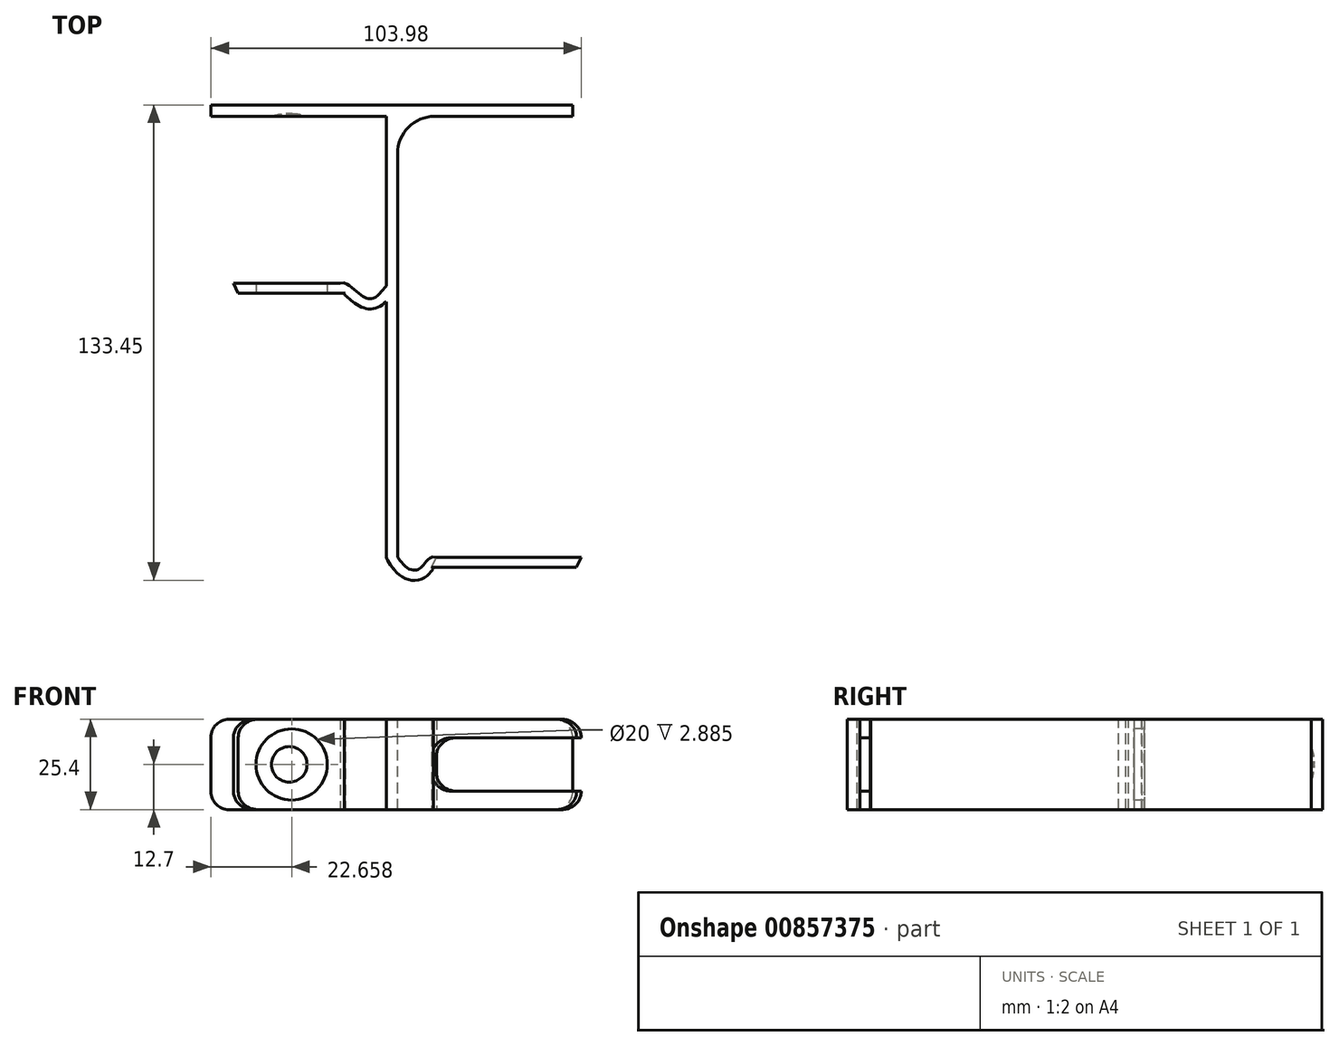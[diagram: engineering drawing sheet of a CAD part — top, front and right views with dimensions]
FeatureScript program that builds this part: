
annotation { "Feature Type Name" : "Feature", "Feature Type Description" : "" }
export const myFeature = defineFeature(function(context is Context, id is Id, definition is map)
    precondition{}
    {
        {
            var Q0;
            Q0=qCreatedBy(makeId("Top.planeOp"),FACE);
            var sketch = newSketch(context, id + "F0", { "sketchPlane" : qUnion([Q0])});
            skLineSegment(sketch, "E0.bottom", {"start": v(-50.8, 12.7) * mm, "end": v(50.8, 12.7) * mm});
            skLineSegment(sketch, "E0.top", {"start": v(-50.8, -12.7) * mm, "end": v(50.8, -12.7) * mm});
            skLineSegment(sketch, "E0.left", {"start": v(-50.8, 12.7) * mm, "end": v(-50.8, -12.7) * mm});
            skLineSegment(sketch, "E0.right", {"start": v(50.8, 12.7) * mm, "end": v(50.8, -12.7) * mm});
            skSolve(sketch);
        }
        {
            var Q0;
            Q0=makeQuery(id+"F0.imprint","IMPRINT",FACE,{"disambiguationData":[TD([[makeQuery(id+"F0.imprint","IMPRINT",EDGE,{"derivedFrom":sQuery(id+"F0.wireOp",EDGE,"E0.bottom")}),-1.0]])]});
            var sketch = newSketch(context, id + "F1", { "sketchPlane" : qUnion([Q0])});
            skLineSegment(sketch, "E1.bottom", {"start": v(-1.59, 12.7) * mm, "end": v(1.59, 12.7) * mm});
            skLineSegment(sketch, "E1.top", {"start": v(-1.59, -12.7) * mm, "end": v(1.59, -12.7) * mm});
            skLineSegment(sketch, "E1.left", {"start": v(-1.59, 12.7) * mm, "end": v(-1.59, -12.7) * mm});
            skLineSegment(sketch, "E1.right", {"start": v(1.59, 12.7) * mm, "end": v(1.59, -12.7) * mm});
            skSolve(sketch);
        }
        {
            var Q0;
            Q0=qCreatedBy(makeId("Front.planeOp"),FACE);
            var sketch = newSketch(context, id + "F2", { "sketchPlane" : qUnion([Q0])});
            skLineSegment(sketch, "E2", {"start": v(0, 0) * mm, "end": v(0, 127) * mm});
            skFitSpline(sketch, "E3", {"points": [v(0, 127) * mm, v(3.55, 131.12) * mm, v(8.81, 131.14) * mm, v(11.88, 128.39) * mm], "startDerivative": vector(1.99, 4.33) * mm, "endDerivative": vector(8.55, 0) * mm});
            skLineSegment(sketch, "E4", {"start": v(11.88, 128.39) * mm, "end": v(52.52, 128.39) * mm});
            skSolve(sketch);
        }
        {
            var Q0;
            Q0=qCreatedBy(makeId("Front.planeOp"),FACE);
            var sketch = newSketch(context, id + "F3", { "sketchPlane" : qUnion([Q0])});
            skLineSegment(sketch, "E5.MirrorCS", {"start": v(-13.8, 51.45) * mm, "end": v(-43.8, 51.45) * mm});
            skFitSpline(sketch, "E6.MirrorCS", {"points": [v(0, 50.8) * mm, v(-3.55, 54.92) * mm, v(-8.81, 54.94) * mm, v(-13.8, 51.45) * mm], "startDerivative": vector(-1.99, 4.33) * mm, "endDerivative": vector(-8.55, 0) * mm});
            skLineSegment(sketch, "E7", {"start": v(0, 50.8) * mm, "end": v(0, 0) * mm});
            skSolve(sketch);
        }
        {
            var Q0;
            Q0 = qSketchRegion(id + "F1", true);
            var Q1;
            Q1=sQuery(id+"F2.wireOp",EDGE,"E2");
            sweep(context, id + "F4", {"profiles" : qUnion([Q0]), "path" : qUnion([Q1])});
        }
        {
            var Q0;
            Q0=makeQuery(id+"F4.opSweep","CAP_FACE",FACE,{"disambiguationData":[OSD([sQuery(id+"F1.wireOp",EDGE,"E1.bottom"),sQuery(id+"F1.wireOp",EDGE,"E1.top"),sQuery(id+"F1.wireOp",EDGE,"E1.left"),sQuery(id+"F1.wireOp",EDGE,"E1.right"),sQuery(id+"F2.wireOp",VERTEX,"E2.end")])],"isStart":false});
            var Q1;
            Q1=sQuery(id+"F2.wireOp",EDGE,"E3");
            var Q2;
            Q2=sQuery(id+"F2.wireOp",EDGE,"E4");
            sweep(context, id + "F5", {"operationType" : NewBodyOperationType.ADD, "profiles" : qUnion([Q0]), "path" : qUnion([Q1, Q2])});
        }
        {
            var Q0;
            Q0 = qSketchRegion(id + "F1", true);
            var Q1;
            Q1=sQuery(id+"F3.wireOp",EDGE,"E7");
            sweep(context, id + "F6", {"profiles" : qUnion([Q0]), "path" : qUnion([Q1])});
        }
        {
            var Q0;
            Q0=makeQuery(id+"F6.opSweep","CAP_FACE",FACE,{"disambiguationData":[OSD([sQuery(id+"F1.wireOp",EDGE,"E1.bottom"),sQuery(id+"F1.wireOp",EDGE,"E1.top"),sQuery(id+"F1.wireOp",EDGE,"E1.left"),sQuery(id+"F1.wireOp",EDGE,"E1.right"),sQuery(id+"F3.wireOp",VERTEX,"E7.start")])],"isStart":false});
            var Q1;
            Q1=sQuery(id+"F3.wireOp",EDGE,"E6.MirrorCS");
            var Q2;
            Q2=sQuery(id+"F3.wireOp",EDGE,"E5.MirrorCS");
            sweep(context, id + "F7", {"operationType" : NewBodyOperationType.ADD, "profiles" : qUnion([Q0]), "path" : qUnion([Q1, Q2])});
        }
        {
            var Q0;
            Q0 = qSketchRegion(id + "F0", true);
            extrude(context, id + "F8", {"entities" : qUnion([Q0]), "depth" : 3.17 * mm, "offsetDistance" : 25.4 * mm});
        }
        {
            var Q0;
            Q0=makeQuery(id+"F7.opSweep","SWEPT_FACE",FACE,{"disambiguationData":[OSD([sQuery(id+"F1.wireOp",EDGE,"E1.right"),sQuery(id+"F3.wireOp",VERTEX,"E7.start"),sQuery(id+"F3.wireOp",EDGE,"E5.MirrorCS")])]});
            var sketch = newSketch(context, id + "F9", { "sketchPlane" : qUnion([Q0])});
            skCircle(sketch, "E8", {"center": v(-28.14, 0) * mm, "radius": 10 * mm});
            skLineSegment(sketch, "E9", {"start": v(-43.14, 0) * mm, "end": v(-13.14, 0) * mm, "construction": true});
            skSolve(sketch);
        }
        {
            var Q0;
            Q0=makeQuery(id+"F9.imprint","IMPRINT",FACE,{"disambiguationData":[TD([[makeQuery(id+"F9.imprint","IMPRINT",EDGE,{"derivedFrom":sQuery(id+"F9.wireOp",EDGE,"E8")}),1.0]])]});
            extrude(context, id + "F10", {"entities" : qUnion([Q0]), "operationType" : NewBodyOperationType.REMOVE, "oppositeDirection" : true, "depth" : 3.33 * mm, "offsetDistance" : 25.4 * mm});
        }
        {
            var Q0;
            Q0=qCreatedBy(makeId("Front.planeOp"),FACE);
            var sketch = newSketch(context, id + "F11", { "sketchPlane" : qUnion([Q0])});
            skLineSegment(sketch, "E10", {"start": v(-28.8, 51.45) * mm, "end": v(-28.8, 3.18) * mm, "construction": true});
            skSolve(sketch);
        }
        {
            var Q0;
            Q0=makeQuery(id+"F8.opExtrude","CAP_FACE",FACE,{"disambiguationData":[OSD([sQuery(id+"F0.wireOp",EDGE,"E0.bottom"),sQuery(id+"F0.wireOp",EDGE,"E0.top"),sQuery(id+"F0.wireOp",EDGE,"E0.left"),sQuery(id+"F0.wireOp",EDGE,"E0.right"),sQuery(id+"F0.wireOp",EDGE,"Ot2qKh74-6Phr-nM6u-f5VL-bmw23gvkR3ha.bottom"),sQuery(id+"F0.wireOp",EDGE,"Ot2qKh74-6Phr-nM6u-f5VL-bmw23gvkR3ha.top"),sQuery(id+"F0.wireOp",EDGE,"Ot2qKh74-6Phr-nM6u-f5VL-bmw23gvkR3ha.left"),sQuery(id+"F0.wireOp",EDGE,"Ot2qKh74-6Phr-nM6u-f5VL-bmw23gvkR3ha.right")])],"isStart":false});
            var sketch = newSketch(context, id + "F12", { "sketchPlane" : qUnion([Q0])});
            skCircle(sketch, "E11", {"center": v(-28.8, 0) * mm, "radius": 5 * mm});
            skSolve(sketch);
        }
        {
            var Q0;
            Q0=makeQuery(id+"F5.opSweep","CAP_FACE",FACE,{"disambiguationData":[OSD([sQuery(id+"F1.wireOp",EDGE,"E1.bottom"),sQuery(id+"F1.wireOp",EDGE,"E1.top"),sQuery(id+"F1.wireOp",EDGE,"E1.left"),sQuery(id+"F1.wireOp",EDGE,"E1.right"),sQuery(id+"F2.wireOp",VERTEX,"E2.end"),sQuery(id+"F2.wireOp",VERTEX,"E4.end")])],"isStart":false});
            var sketch = newSketch(context, id + "F13", { "sketchPlane" : qUnion([Q0])});
            skLineSegment(sketch, "E12.bottom", {"start": v(-7.5, 96.35) * mm, "end": v(7.5, 96.35) * mm});
            skLineSegment(sketch, "E12.top", {"start": v(-7.5, 93.17) * mm, "end": v(7.5, 93.17) * mm});
            skLineSegment(sketch, "E12.left", {"start": v(-7.5, 96.35) * mm, "end": v(-7.5, 93.17) * mm});
            skLineSegment(sketch, "E12.right", {"start": v(7.5, 96.35) * mm, "end": v(7.5, 93.17) * mm});
            skLineSegment(sketch, "E13", {"start": v(-12.7, 95.1) * mm, "end": v(-7.5, 95.1) * mm, "construction": true});
            skLineSegment(sketch, "E14", {"start": v(7.5, 95.22) * mm, "end": v(12.7, 95.22) * mm, "construction": true});
            skSolve(sketch);
        }
        {
            var Q0;
            Q0 = qSketchRegion(id + "F13", true);
            var Q1;
            Q1=sQuery(id+"F2.wireOp",EDGE,"E4");
            sweep(context, id + "F14", {"operationType" : NewBodyOperationType.REMOVE, "profiles" : qUnion([Q0]), "path" : qUnion([Q1])});
        }
        {
            var Q0;
            Q0=qCreatedBy(makeId("Front.planeOp"),FACE);
            var sketch = newSketch(context, id + "F15", { "sketchPlane" : qUnion([Q0])});
            skLineSegment(sketch, "E15", {"start": v(-28.8, 3.18) * mm, "end": v(-28.8, 2.44) * mm});
            skFitSpline(sketch, "E16", {"points": [v(-28.8, 2.44) * mm, v(-27.06, 2.43) * mm, v(-25.7, 2.64) * mm, v(-23.8, 3.18) * mm], "startDerivative": vector(3.42, -0.31) * mm, "endDerivative": vector(2.6, 1.1) * mm});
            skLineSegment(sketch, "E17", {"start": v(-28.8, 3.18) * mm, "end": v(-23.8, 3.18) * mm});
            skSolve(sketch);
        }
        {
            var Q0;
            Q0 = qSketchRegion(id + "F15", true);
            var Q1;
            Q1=sQuery(id+"F15.wireOp",EDGE,"E15");
            revolve(context, id + "F16", {"operationType" : NewBodyOperationType.REMOVE, "surfaceOperationType" : NewSurfaceOperationType.NEW, "entities" : qUnion([Q0]), "axis" : qUnion([Q1]), "revolveType" : RevolveType.FULL, "oppositeDirection" : true});
        }
        {
            var Q0;
            Q0=makeQuery(id+"F8.opExtrude","SWEPT_BODY",BODY,{"disambiguationData":[OSD([sQuery(id+"F0.wireOp",EDGE,"E0.bottom"),sQuery(id+"F0.wireOp",EDGE,"E0.top"),sQuery(id+"F0.wireOp",EDGE,"E0.left"),sQuery(id+"F0.wireOp",EDGE,"E0.right")])]});
            var Q1;
            Q1=makeQuery(id+"F6.opSweep","SWEPT_BODY",BODY,{"disambiguationData":[OSD([sQuery(id+"F1.wireOp",EDGE,"E1.bottom"),sQuery(id+"F1.wireOp",EDGE,"E1.top"),sQuery(id+"F1.wireOp",EDGE,"E1.left"),sQuery(id+"F1.wireOp",EDGE,"E1.right"),sQuery(id+"F3.wireOp",EDGE,"E7")])]});
            var Q2;
            Q2=makeQuery(id+"F4.opSweep","SWEPT_BODY",BODY,{"disambiguationData":[OSD([sQuery(id+"F1.wireOp",EDGE,"E1.bottom"),sQuery(id+"F1.wireOp",EDGE,"E1.top"),sQuery(id+"F1.wireOp",EDGE,"E1.left"),sQuery(id+"F1.wireOp",EDGE,"E1.right"),sQuery(id+"F2.wireOp",EDGE,"E2")])]});
            var Q3;
            Q3=sQuery(id+"F0.wireOp",EDGE,"E0.top");
            transform(context, id + "F17", {"entities" : qUnion([Q0, Q1, Q2]), "transformType" : TransformType.ROTATION, "transformAxis" : qUnion([Q3]), "angle" : 90 * degree, "makeCopy" : false});
        }
        {
            var Q0;
            Q0=makeQuery(id+"F8.opExtrude","SWEPT_BODY",BODY,{"disambiguationData":[OSD([sQuery(id+"F0.wireOp",EDGE,"E0.bottom"),sQuery(id+"F0.wireOp",EDGE,"E0.top"),sQuery(id+"F0.wireOp",EDGE,"E0.left"),sQuery(id+"F0.wireOp",EDGE,"E0.right")])]});
            var Q1;
            Q1=makeQuery(id+"F6.opSweep","SWEPT_BODY",BODY,{"disambiguationData":[OSD([sQuery(id+"F1.wireOp",EDGE,"E1.bottom"),sQuery(id+"F1.wireOp",EDGE,"E1.top"),sQuery(id+"F1.wireOp",EDGE,"E1.left"),sQuery(id+"F1.wireOp",EDGE,"E1.right"),sQuery(id+"F3.wireOp",EDGE,"E7")])]});
            var Q2;
            Q2=makeQuery(id+"F4.opSweep","SWEPT_BODY",BODY,{"disambiguationData":[OSD([sQuery(id+"F1.wireOp",EDGE,"E1.bottom"),sQuery(id+"F1.wireOp",EDGE,"E1.top"),sQuery(id+"F1.wireOp",EDGE,"E1.left"),sQuery(id+"F1.wireOp",EDGE,"E1.right"),sQuery(id+"F2.wireOp",EDGE,"E2")])]});
            booleanBodies(context, id + "F18", {"operationType" : BooleanOperationType.UNION, "tools" : qUnion([Q0, Q1, Q2])});
        }
        {
            var Q0;
            Q0=makeQuery(id+"F18.opBoolean","INTERSECT",EDGE,{"derivedFrom":[makeQuery(id+"F4.opSweep","SWEPT_FACE",FACE,{"disambiguationData":[OSD([sQuery(id+"F1.wireOp",EDGE,"E1.right"),sQuery(id+"F2.wireOp",EDGE,"E2")])]}),makeQuery(id+"F8.opExtrude","CAP_FACE",FACE,{"disambiguationData":[OSD([sQuery(id+"F0.wireOp",EDGE,"E0.bottom"),sQuery(id+"F0.wireOp",EDGE,"E0.top"),sQuery(id+"F0.wireOp",EDGE,"E0.left"),sQuery(id+"F0.wireOp",EDGE,"E0.right")])],"isStart":false})]});
            var Q1;
            Q1=makeQuery(id+"F18.opBoolean","INTERSECT",EDGE,{"derivedFrom":[makeQuery(id+"F6.opSweep","SWEPT_FACE",FACE,{"disambiguationData":[OSD([sQuery(id+"F1.wireOp",EDGE,"E1.left"),sQuery(id+"F3.wireOp",EDGE,"E7")])]}),makeQuery(id+"F8.opExtrude","CAP_FACE",FACE,{"disambiguationData":[OSD([sQuery(id+"F0.wireOp",EDGE,"E0.bottom"),sQuery(id+"F0.wireOp",EDGE,"E0.top"),sQuery(id+"F0.wireOp",EDGE,"E0.left"),sQuery(id+"F0.wireOp",EDGE,"E0.right")])],"isStart":false})]});
            var Q2;
            Q2=makeQuery(id+"F18.opBoolean","INTERSECT",EDGE,{"derivedFrom":[makeQuery(id+"F4.opSweep","SWEPT_FACE",FACE,{"disambiguationData":[OSD([sQuery(id+"F1.wireOp",EDGE,"E1.left"),sQuery(id+"F2.wireOp",EDGE,"E2")])]}),makeQuery(id+"F7.opSweep","SWEPT_FACE",FACE,{"disambiguationData":[OSD([sQuery(id+"F1.wireOp",EDGE,"E1.right"),sQuery(id+"F3.wireOp",VERTEX,"E7.start"),sQuery(id+"F3.wireOp",EDGE,"E6.MirrorCS")])]})]});
            fillet(context, id + "F19", {"entities" : qUnion([Q0, Q1, Q2]), "radius" : 10.42 * mm, "tangentPropagation" : true, "allowEdgeOverflow" : false});
        }
        {
            var Q0;
            Q0=makeQuery(id+"F14.boolean.opBoolean","COPY",EDGE,{"derivedFrom":makeQuery(id+"F14.opSweep","CAP_EDGE",EDGE,{"disambiguationData":[OSD([sQuery(id+"F2.wireOp",VERTEX,"E4.start"),sQuery(id+"F13.wireOp",EDGE,"E12.left")])],"isStart":false})});
            var Q1;
            Q1=makeQuery(id+"F14.boolean.opBoolean","COPY",EDGE,{"derivedFrom":makeQuery(id+"F14.opSweep","CAP_EDGE",EDGE,{"disambiguationData":[OSD([sQuery(id+"F2.wireOp",VERTEX,"E4.start"),sQuery(id+"F13.wireOp",EDGE,"E12.right")])],"isStart":false})});
            fillet(context, id + "F20", {"entities" : qUnion([Q0, Q1]), "radius" : 5.08 * mm, "tangentPropagation" : true, "allowEdgeOverflow" : false});
        }
        {
            var Q0;
            Q0=makeQuery(id+"F8.opExtrude","SWEPT_EDGE",EDGE,{"disambiguationData":[OSD([sQuery(id+"F0.wireOp",EDGE,"E0.top"),sQuery(id+"F0.wireOp",EDGE,"E0.right")])]});
            var Q1;
            Q1=makeQuery(id+"F8.opExtrude","SWEPT_EDGE",EDGE,{"disambiguationData":[OSD([sQuery(id+"F0.wireOp",EDGE,"E0.bottom"),sQuery(id+"F0.wireOp",EDGE,"E0.right")])]});
            var Q2;
            Q2=makeQuery(id+"F5.opSweep","CAP_EDGE",EDGE,{"disambiguationData":[OSD([sQuery(id+"F1.wireOp",EDGE,"E1.top"),sQuery(id+"F2.wireOp",VERTEX,"E2.end"),sQuery(id+"F2.wireOp",VERTEX,"E4.end")])],"isStart":false});
            var Q3;
            Q3=makeQuery(id+"F5.opSweep","CAP_EDGE",EDGE,{"disambiguationData":[OSD([sQuery(id+"F1.wireOp",EDGE,"E1.bottom"),sQuery(id+"F2.wireOp",VERTEX,"E2.end"),sQuery(id+"F2.wireOp",VERTEX,"E4.end")])],"isStart":false});
            var Q4;
            Q4=makeQuery(id+"F8.opExtrude","SWEPT_EDGE",EDGE,{"disambiguationData":[OSD([sQuery(id+"F0.wireOp",EDGE,"E0.top"),sQuery(id+"F0.wireOp",EDGE,"E0.left")])]});
            var Q5;
            Q5=makeQuery(id+"F8.opExtrude","SWEPT_EDGE",EDGE,{"disambiguationData":[OSD([sQuery(id+"F0.wireOp",EDGE,"E0.bottom"),sQuery(id+"F0.wireOp",EDGE,"E0.left")])]});
            var Q6;
            Q6=makeQuery(id+"F7.opSweep","CAP_EDGE",EDGE,{"disambiguationData":[OSD([sQuery(id+"F1.wireOp",EDGE,"E1.bottom"),sQuery(id+"F3.wireOp",VERTEX,"E5.MirrorCS.end"),sQuery(id+"F3.wireOp",VERTEX,"E7.start")])],"isStart":false});
            var Q7;
            Q7=makeQuery(id+"F7.opSweep","CAP_EDGE",EDGE,{"disambiguationData":[OSD([sQuery(id+"F1.wireOp",EDGE,"E1.top"),sQuery(id+"F3.wireOp",VERTEX,"E5.MirrorCS.end"),sQuery(id+"F3.wireOp",VERTEX,"E7.start")])],"isStart":false});
            fillet(context, id + "F21", {"entities" : qUnion([Q0, Q1, Q2, Q3, Q4, Q5, Q6, Q7]), "radius" : 5.08 * mm, "tangentPropagation" : true, "allowEdgeOverflow" : false});
        }
    });
